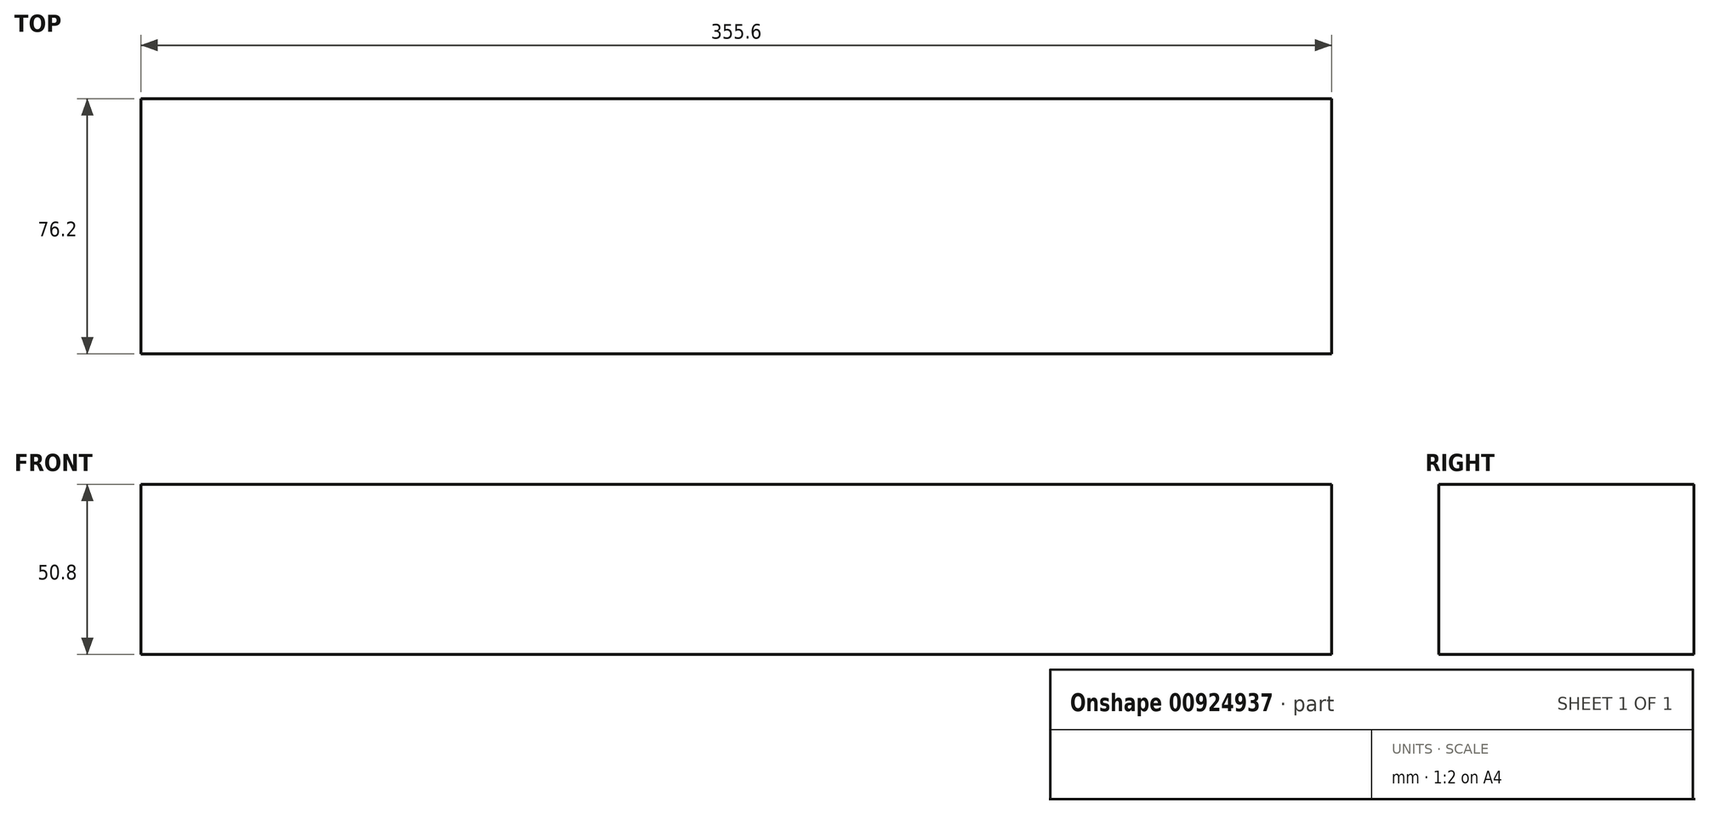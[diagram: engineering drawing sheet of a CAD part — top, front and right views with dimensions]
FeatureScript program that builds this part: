
annotation { "Feature Type Name" : "Feature", "Feature Type Description" : "" }
export const myFeature = defineFeature(function(context is Context, id is Id, definition is map)
    precondition{}
    {
        {
            var Q0;
            Q0=qCreatedBy(makeId("Top.planeOp"),FACE);
            var sketch = newSketch(context, id + "F0", { "sketchPlane" : qUnion([Q0])});
            skLineSegment(sketch, "E0.bottom", {"start": v(-177.8, 38.1) * mm, "end": v(177.8, 38.1) * mm});
            skLineSegment(sketch, "E0.top", {"start": v(-177.8, -38.1) * mm, "end": v(177.8, -38.1) * mm});
            skLineSegment(sketch, "E0.left", {"start": v(-177.8, 38.1) * mm, "end": v(-177.8, -38.1) * mm});
            skLineSegment(sketch, "E0.right", {"start": v(177.8, 38.1) * mm, "end": v(177.8, -38.1) * mm});
            skSolve(sketch);
        }
        {
            var Q0;
            Q0=makeQuery(id+"F0.imprint","IMPRINT",FACE,{"disambiguationData":[TD([[makeQuery(id+"F0.imprint","IMPRINT",EDGE,{"derivedFrom":sQuery(id+"F0.wireOp",EDGE,"E0.bottom")}),-1.0]])]});
            extrude(context, id + "F1", {"entities" : qUnion([Q0]), "depth" : 50.8 * mm, "offsetDistance" : 25.4 * mm});
        }
    });
